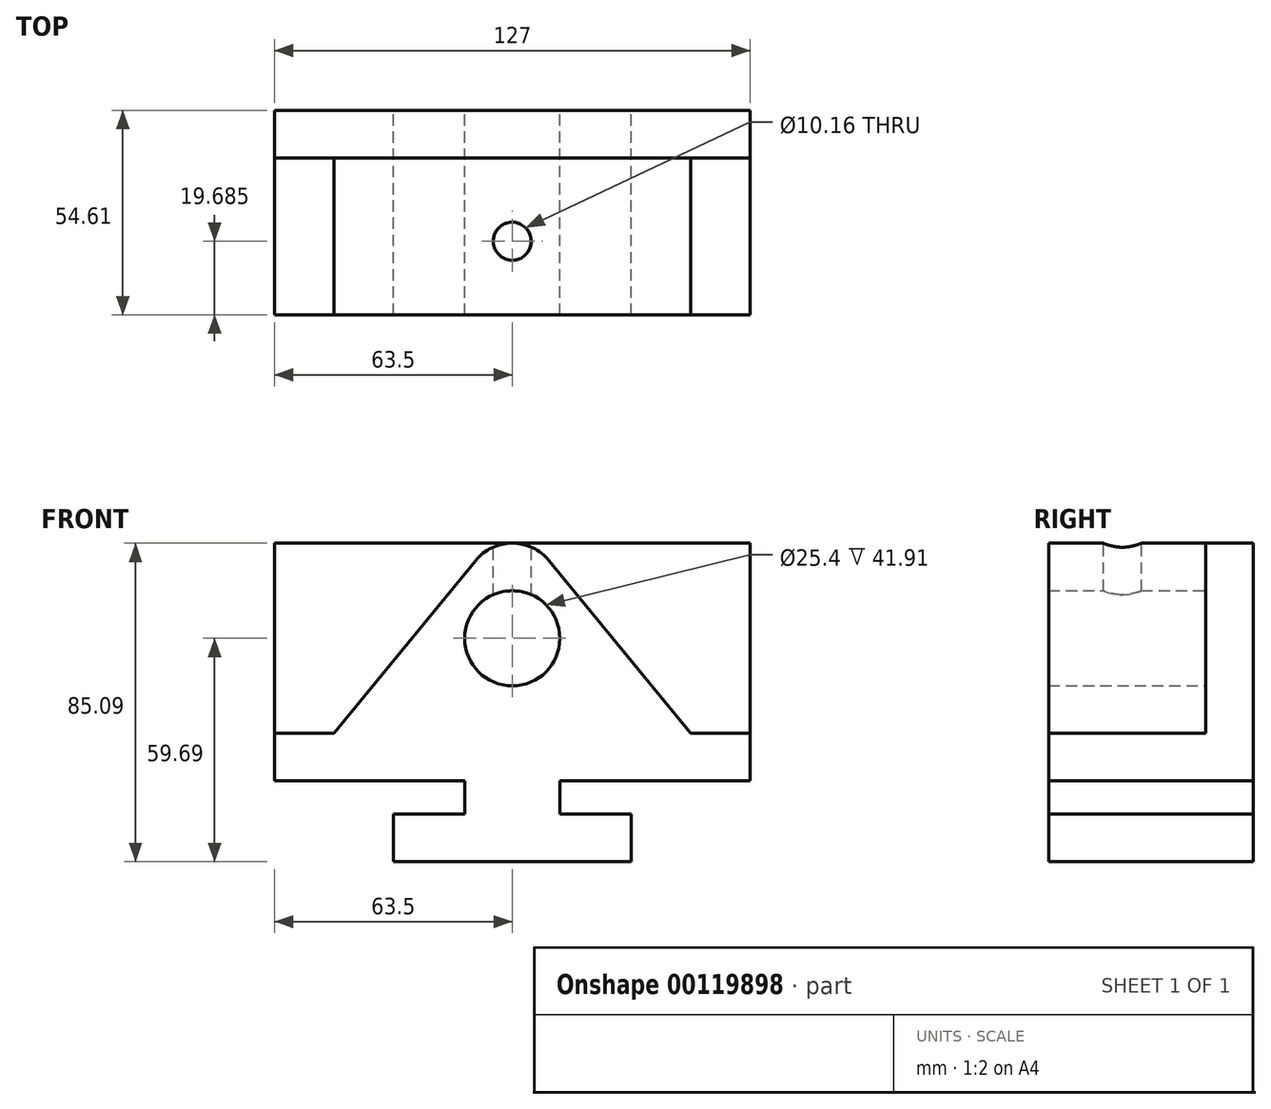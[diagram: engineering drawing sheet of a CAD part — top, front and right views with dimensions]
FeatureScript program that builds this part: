
annotation { "Feature Type Name" : "Feature", "Feature Type Description" : "" }
export const myFeature = defineFeature(function(context is Context, id is Id, definition is map)
    precondition{}
    {
        {
            var Q0;
            Q0=qCreatedBy(makeId("Front.planeOp"),FACE);
            var sketch = newSketch(context, id + "F0", { "sketchPlane" : qUnion([Q0])});
            skLineSegment(sketch, "E0", {"start": v(0, 85.1) * mm, "end": v(0, -26.54) * mm, "construction": true});
            skLineSegment(sketch, "E1", {"start": v(0, 0) * mm, "end": v(-31.75, 0) * mm});
            skLineSegment(sketch, "E2", {"start": v(-31.75, 0) * mm, "end": v(-31.75, 12.7) * mm});
            skLineSegment(sketch, "E3", {"start": v(-31.75, 12.7) * mm, "end": v(-12.7, 12.7) * mm});
            skLineSegment(sketch, "E4", {"start": v(-12.7, 12.7) * mm, "end": v(-12.7, 21.59) * mm});
            skLineSegment(sketch, "E5", {"start": v(-12.7, 21.59) * mm, "end": v(-63.5, 21.59) * mm});
            skLineSegment(sketch, "E6", {"start": v(-63.5, 21.59) * mm, "end": v(-63.5, 34.29) * mm});
            skLineSegment(sketch, "E7", {"start": v(-63.5, 34.3) * mm, "end": v(-47.63, 34.3) * mm});
            skLineSegment(sketch, "E8", {"start": v(-47.63, 34.3) * mm, "end": v(-9.82, 80.44) * mm});
            skArc(sketch, "E9", {"start": v(-9.82, 80.44) * mm, "mid": v(-5.44, 83.87) * mm, "end": v(0, 85.1) * mm});
            skLineSegment(sketch, "E10", {"start": v(-67.57, 0) * mm, "end": v(77.25, 0) * mm, "construction": true});
            skLineSegment(sketch, "E11", {"start": v(-63.5, 34.29) * mm, "end": v(-63.5, 85.1) * mm});
            skLineSegment(sketch, "E12", {"start": v(-63.5, 85.1) * mm, "end": v(0, 85.1) * mm});
            skArc(sketch, "E13.MirrorCS", {"start": v(9.82, 80.44) * mm, "mid": v(5.44, 83.87) * mm, "end": v(0, 85.1) * mm});
            skLineSegment(sketch, "E14.MirrorCS", {"start": v(63.5, 85.1) * mm, "end": v(0, 85.1) * mm});
            skLineSegment(sketch, "E15.MirrorCS", {"start": v(47.63, 34.3) * mm, "end": v(9.82, 80.44) * mm});
            skLineSegment(sketch, "E16.MirrorCS", {"start": v(63.5, 34.29) * mm, "end": v(63.5, 85.1) * mm});
            skLineSegment(sketch, "E17.MirrorCS", {"start": v(63.5, 34.3) * mm, "end": v(47.63, 34.3) * mm});
            skLineSegment(sketch, "E18.MirrorCS", {"start": v(63.5, 21.59) * mm, "end": v(63.5, 34.29) * mm});
            skLineSegment(sketch, "E19.MirrorCS", {"start": v(12.7, 21.59) * mm, "end": v(63.5, 21.59) * mm});
            skLineSegment(sketch, "E20.MirrorCS", {"start": v(12.7, 12.7) * mm, "end": v(12.7, 21.59) * mm});
            skLineSegment(sketch, "E21.MirrorCS", {"start": v(31.75, 12.7) * mm, "end": v(12.7, 12.7) * mm});
            skLineSegment(sketch, "E22.MirrorCS", {"start": v(31.75, 0) * mm, "end": v(31.75, 12.7) * mm});
            skLineSegment(sketch, "E23.MirrorCS", {"start": v(0, 0) * mm, "end": v(31.75, 0) * mm});
            skCircle(sketch, "E24", {"center": v(0, 59.7) * mm, "radius": 12.7 * mm});
            skSolve(sketch);
        }
        {
            var Q0;
            Q0=makeQuery(id+"F0.imprint","IMPRINT",FACE,{"disambiguationData":[TD([[makeQuery(id+"F0.imprint","IMPRINT",EDGE,{"derivedFrom":sQuery(id+"F0.wireOp",EDGE,"E1")}),-1.0]])]});
            extrude(context, id + "F1", {"entities" : qUnion([Q0]), "depth" : 54.6 * mm});
        }
        {
            var Q0;
            Q0=makeQuery(id+"F0.imprint","IMPRINT",FACE,{"disambiguationData":[TD([[makeQuery(id+"F0.imprint","IMPRINT",EDGE,{"derivedFrom":sQuery(id+"F0.wireOp",EDGE,"E24")}),1.0]])]});
            extrude(context, id + "F2", {"entities" : qUnion([Q0]), "operationType" : NewBodyOperationType.ADD, "depth" : 12.7 * mm});
        }
        {
            var Q0;
            Q0=makeQuery(id+"F0.imprint","IMPRINT",FACE,{"disambiguationData":[TD([[makeQuery(id+"F0.imprint","IMPRINT",EDGE,{"derivedFrom":sQuery(id+"F0.wireOp",EDGE,"E7")}),1.0]])]});
            var Q1;
            Q1=makeQuery(id+"F0.imprint","IMPRINT",FACE,{"disambiguationData":[TD([[makeQuery(id+"F0.imprint","IMPRINT",EDGE,{"derivedFrom":sQuery(id+"F0.wireOp",EDGE,"E13.MirrorCS")}),-1.0]])]});
            extrude(context, id + "F3", {"entities" : qUnion([Q0, Q1]), "operationType" : NewBodyOperationType.ADD, "depth" : 12.7 * mm});
        }
        {
            var Q0;
            Q0=makeQuery(id+"F3.boolean.opBoolean","MERGE",FACE,{"derivedFrom":[makeQuery(id+"F3.opExtrude","SWEPT_FACE",FACE,{"disambiguationData":[OSD([sQuery(id+"F0.wireOp",EDGE,"E12")])]}),makeQuery(id+"F3.opExtrude","SWEPT_FACE",FACE,{"disambiguationData":[OSD([sQuery(id+"F0.wireOp",EDGE,"E14.MirrorCS")])]})]});
            var sketch = newSketch(context, id + "F4", { "sketchPlane" : qUnion([Q0])});
            skLineSegment(sketch, "E25", {"start": v(0, 31.24) * mm, "end": v(0, -74.78) * mm, "construction": true});
            skPoint(sketch, "E25.startSnap0", {"position": v(0, 0) * mm});
            skCircle(sketch, "E26", {"center": v(0, -34.93) * mm, "radius": 5.08 * mm});
            skSolve(sketch);
        }
        {
            var Q0;
            Q0=makeQuery(id+"F4.imprint","IMPRINT",FACE,{"disambiguationData":[TD([[makeQuery(id+"F4.imprint","IMPRINT",EDGE,{"derivedFrom":sQuery(id+"F4.wireOp",EDGE,"E26")}),1.0]])]});
            extrude(context, id + "F5", {"entities" : qUnion([Q0]), "operationType" : NewBodyOperationType.REMOVE, "oppositeDirection" : true, "depth" : 19.05 * mm});
        }
    });
